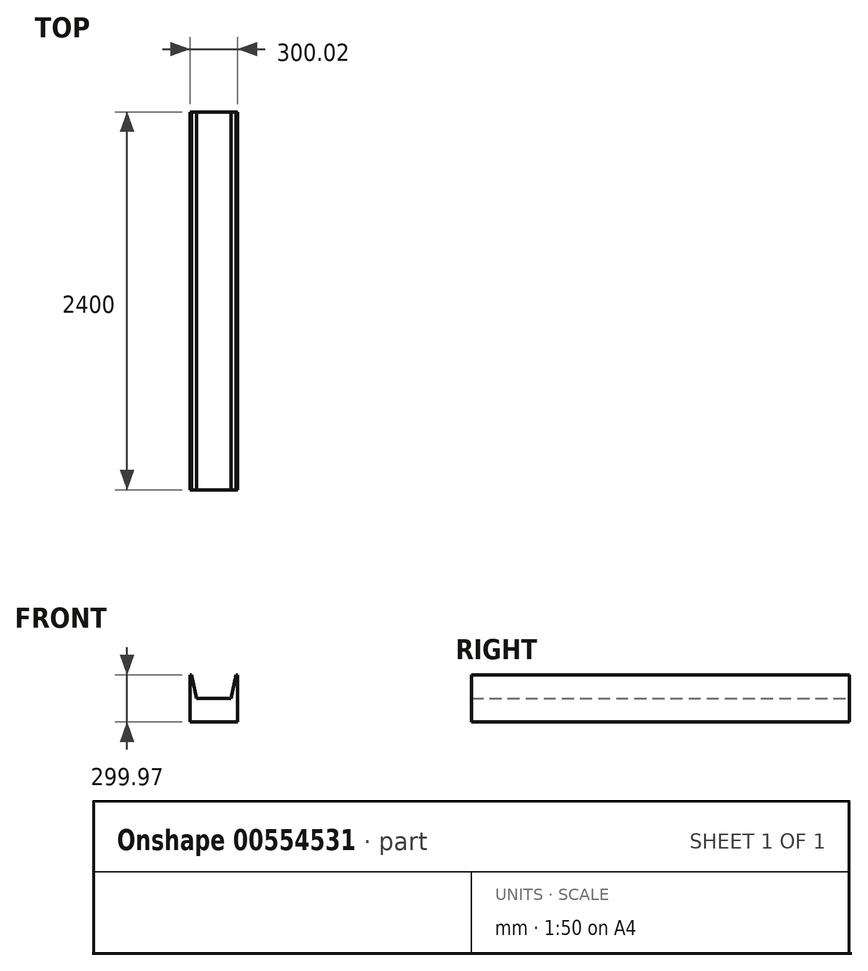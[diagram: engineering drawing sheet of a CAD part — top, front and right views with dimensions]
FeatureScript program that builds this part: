
annotation { "Feature Type Name" : "Feature", "Feature Type Description" : "" }
export const myFeature = defineFeature(function(context is Context, id is Id, definition is map)
    precondition{}
    {
        {
            var Q0;
            Q0=qCreatedBy(makeId("Front.planeOp"),FACE);
            var sketch = newSketch(context, id + "F0", { "sketchPlane" : qUnion([Q0])});
            skLineSegment(sketch, "E0", {"start": v(-300.61, -39.47) * mm, "end": v(-0.61, -39.47) * mm});
            skLineSegment(sketch, "E1", {"start": v(-0.61, -39.47) * mm, "end": v(-0.61, 260.5) * mm});
            skLineSegment(sketch, "E2", {"start": v(-40.42, 110.13) * mm, "end": v(-260.6, 110.13) * mm});
            skLineSegment(sketch, "E3", {"start": v(-300.63, 260.5) * mm, "end": v(-300.61, -39.47) * mm});
            skLineSegment(sketch, "E4", {"start": v(-300.63, 260.5) * mm, "end": v(-290.15, 260.5) * mm});
            skLineSegment(sketch, "E5", {"start": v(-0.61, 260.5) * mm, "end": v(-10.16, 260.5) * mm});
            skLineSegment(sketch, "E6", {"start": v(-10.16, 260.5) * mm, "end": v(-40.42, 110.13) * mm});
            skLineSegment(sketch, "E7", {"start": v(-290.15, 260.5) * mm, "end": v(-260.6, 110.13) * mm});
            skSolve(sketch);
        }
        {
            var Q0;
            Q0=makeQuery(id+"F0.imprint","IMPRINT",FACE,{"disambiguationData":[TD([[makeQuery(id+"F0.imprint","IMPRINT",EDGE,{"derivedFrom":sQuery(id+"F0.wireOp",EDGE,"E0")}),1.0]])]});
            extrude(context, id + "F1", {"entities" : qUnion([Q0]), "depth" : 2400 * mm, "offsetDistance" : 25 * mm});
        }
    });
